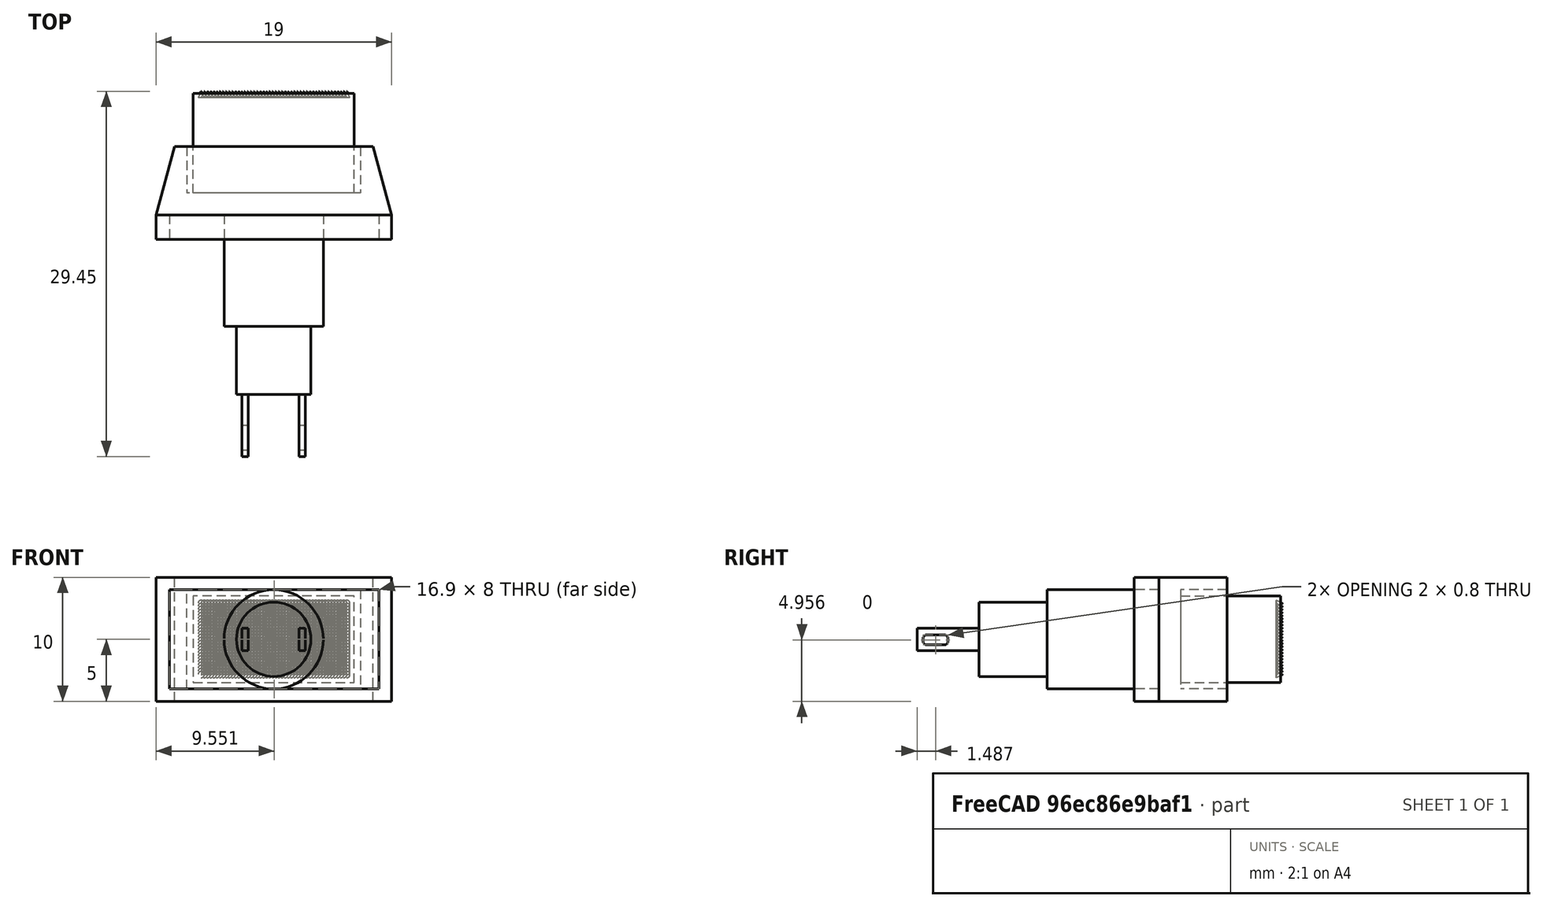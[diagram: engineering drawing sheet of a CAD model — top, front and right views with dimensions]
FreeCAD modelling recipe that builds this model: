
FCSTD DOCUMENT  (FreeCAD 0.18R16110 (Git))
Label: Miyama DS-462 2
License: All rights reserved
LicenseURL: http://en.wikipedia.org/wiki/All_rights_reserved
objects: Sketcher::SketchObject×11, Part::Extrusion×8, Part::Cut×3, Part::Cone×1, Part::FeaturePython×1, Part::Sweep×1
note: 25 computed .brp shape members not serialized (recipe doc carries the construction recipe); baked Part::Feature solids carry a one-line shape summary decoded from their .brp

FEATURE [Sketcher::SketchObject] Sketch
  sketch-geometry (12):
    g0: LineSegment [constr] StartX=-7 StartY=11.8 StartZ=0 EndX=7 EndY=11.8 EndZ=0
    g1: LineSegment [constr] StartX=-9.5 StartY=0 StartZ=0 EndX=9.5 EndY=0 EndZ=0
    g2: LineSegment [constr] StartX=-7 StartY=11.8 StartZ=0 EndX=-7 EndY=7.5 EndZ=0
    g3: LineSegment [constr] StartX=7 StartY=7.5 StartZ=0 EndX=7 EndY=11.8 EndZ=0
    g4: LineSegment [constr] StartX=9.5 StartY=0 StartZ=0 EndX=9.5 EndY=2 EndZ=0
    g5: LineSegment [constr] StartX=9.5 StartY=2 StartZ=0 EndX=7 EndY=7.5 EndZ=0
    g6: LineSegment [constr] StartX=-9.5 StartY=0 StartZ=0 EndX=-9.5 EndY=2 EndZ=0
    g7: LineSegment [constr] StartX=-9.5 StartY=2 StartZ=0 EndX=-7 EndY=7.5 EndZ=0
    g8: LineSegment StartX=-9.5 StartY=2 StartZ=0 EndX=-9.5 EndY=0 EndZ=0
    g9: LineSegment StartX=-9.5 StartY=0 StartZ=0 EndX=9.5 EndY=0 EndZ=0
    g10: LineSegment StartX=9.5 StartY=0 StartZ=0 EndX=9.5 EndY=2 EndZ=0
    g11: LineSegment StartX=9.5 StartY=2 StartZ=0 EndX=-9.5 EndY=2 EndZ=0
  constraints (31):
    c: DistanceX(g0,g0) = 14
    c: DistanceX(g1,g1) = 19
    c: Symmetric(g0,g0,g-2)
    c: Coincident(g2,g0)
    c: Vertical(g2)
    c: Coincident(g3,g0)
    c: Vertical(g3)
    c: DistanceY(g3,g3) = 4.3
    c: Coincident(g4,g1)
    c: Coincident(g5,g4)
    c: Coincident(g7,g6)
    c: Coincident(g7,g2)
    c: Vertical(g6)
    c: Vertical(g4)
    c: DistanceY(g1,g5) = 7.5
    c: Equal(g4,g6)
    c: Coincident(g6,g1)
    c: DistanceY(g4,g4) = 2
    c: PointOnObject(g-1,g1)
    c: Horizontal(g1)
    c: Equal(g7,g5)
    c: Coincident(g3,g5)
    c: Equal(g3,g2)
    c: Coincident(g6,g8)
    c: Coincident(g8,g1)
    c: Coincident(g8,g9)
    c: Coincident(g9,g1)
    c: Coincident(g9,g10)
    c: Coincident(g10,g4)
    c: Coincident(g10,g11)
    c: Coincident(g11,g8)
FEATURE [Sketcher::SketchObject] Sketch001
  sketch-geometry (12):
    g0: LineSegment [constr] StartX=-8 StartY=11.8 StartZ=0 EndX=8 EndY=11.8 EndZ=0
    g1: LineSegment [constr] StartX=-9.5 StartY=0 StartZ=0 EndX=9.5 EndY=0 EndZ=0
    g2: LineSegment [constr] StartX=-8 StartY=11.8 StartZ=0 EndX=-8 EndY=7.5 EndZ=0
    g3: LineSegment [constr] StartX=8 StartY=7.5 StartZ=0 EndX=8 EndY=11.8 EndZ=0
    g4: LineSegment [constr] StartX=9.5 StartY=0 StartZ=0 EndX=9.5 EndY=2 EndZ=0
    g5: LineSegment [constr] StartX=9.5 StartY=2 StartZ=0 EndX=8 EndY=7.5 EndZ=0
    g6: LineSegment [constr] StartX=-9.5 StartY=0 StartZ=0 EndX=-9.5 EndY=2 EndZ=0
    g7: LineSegment [constr] StartX=-9.5 StartY=2 StartZ=0 EndX=-8 EndY=7.5 EndZ=0
    g8: LineSegment StartX=-9.5 StartY=2 StartZ=0 EndX=-8 EndY=7.5 EndZ=0
    g9: LineSegment StartX=-8 StartY=7.5 StartZ=0 EndX=8 EndY=7.5 EndZ=0
    g10: LineSegment StartX=8 StartY=7.5 StartZ=0 EndX=9.5 EndY=2 EndZ=0
    g11: LineSegment StartX=9.5 StartY=2 StartZ=0 EndX=-9.5 EndY=2 EndZ=0
  constraints (31):
    c: DistanceX(g0,g0) = 16
    c: DistanceX(g1,g1) = 19
    c: Symmetric(g0,g0,g-2)
    c: Coincident(g2,g0)
    c: Vertical(g2)
    c: Coincident(g3,g0)
    c: Vertical(g3)
    c: DistanceY(g3,g3) = 4.3
    c: Coincident(g4,g1)
    c: Coincident(g5,g4)
    c: Coincident(g7,g6)
    c: Coincident(g7,g2)
    c: Vertical(g6)
    c: Vertical(g4)
    c: DistanceY(g1,g5) = 7.5
    c: Equal(g4,g6)
    c: Coincident(g6,g1)
    c: DistanceY(g4,g4) = 2
    c: PointOnObject(g-1,g1)
    c: Horizontal(g1)
    c: Equal(g7,g5)
    c: Coincident(g3,g5)
    c: Equal(g3,g2)
    c: Coincident(g6,g8)
    c: Coincident(g8,g2)
    c: Coincident(g8,g9)
    c: Coincident(g9,g10)
    c: Coincident(g10,g4)
    c: Coincident(g10,g11)
    c: Coincident(g11,g8)
    c: Coincident(g9,g3)
FEATURE [Sketcher::SketchObject] Sketch002
  sketch-geometry (12):
    g0: LineSegment [constr] StartX=-7 StartY=11.8 StartZ=0 EndX=7 EndY=11.8 EndZ=0
    g1: LineSegment [constr] StartX=-9.5 StartY=0 StartZ=0 EndX=9.5 EndY=0 EndZ=0
    g2: LineSegment [constr] StartX=-7 StartY=11.8 StartZ=0 EndX=-7 EndY=7.5 EndZ=0
    g3: LineSegment [constr] StartX=7 StartY=7.5 StartZ=0 EndX=7 EndY=11.8 EndZ=0
    g4: LineSegment [constr] StartX=9.5 StartY=0 StartZ=0 EndX=9.5 EndY=2 EndZ=0
    g5: LineSegment [constr] StartX=9.5 StartY=2 StartZ=0 EndX=7 EndY=7.5 EndZ=0
    g6: LineSegment [constr] StartX=-9.5 StartY=0 StartZ=0 EndX=-9.5 EndY=2 EndZ=0
    g7: LineSegment [constr] StartX=-9.5 StartY=2 StartZ=0 EndX=-7 EndY=7.5 EndZ=0
    g8: LineSegment StartX=-7 StartY=11.8 StartZ=0 EndX=-7 EndY=7.5 EndZ=0
    g9: LineSegment StartX=-7 StartY=7.5 StartZ=0 EndX=7 EndY=7.5 EndZ=0
    g10: LineSegment StartX=7 StartY=7.5 StartZ=0 EndX=7 EndY=11.8 EndZ=0
    g11: LineSegment StartX=7 StartY=11.8 StartZ=0 EndX=-7 EndY=11.8 EndZ=0
  constraints (31):
    c: DistanceX(g0,g0) = 14
    c: DistanceX(g1,g1) = 19
    c: Symmetric(g0,g0,g-2)
    c: Coincident(g2,g0)
    c: Vertical(g2)
    c: Coincident(g3,g0)
    c: Vertical(g3)
    c: DistanceY(g3,g3) = 4.3
    c: Coincident(g4,g1)
    c: Coincident(g5,g4)
    c: Coincident(g7,g6)
    c: Coincident(g7,g2)
    c: Vertical(g6)
    c: Vertical(g4)
    c: DistanceY(g1,g5) = 7.5
    c: Equal(g4,g6)
    c: Coincident(g6,g1)
    c: DistanceY(g4,g4) = 2
    c: PointOnObject(g-1,g1)
    c: Horizontal(g1)
    c: Equal(g7,g5)
    c: Coincident(g3,g5)
    c: Equal(g3,g2)
    c: Coincident(g0,g8)
    c: Coincident(g8,g2)
    c: Coincident(g8,g9)
    c: Coincident(g9,g3)
    c: Coincident(g9,g10)
    c: Coincident(g10,g0)
    c: Coincident(g10,g11)
    c: Coincident(g11,g8)
FEATURE [Part::Extrusion] Extrude
  Base = -> Sketch
  Dir = (0,0,1)
  DirMode = 2
  FaceMakerClass = Part::FaceMakerBullseye
  LengthFwd = 10
  LengthRev = 0
  Solid = true
  Symmetric = false
FEATURE [Part::Extrusion] Extrude001
  Base = -> Sketch001
  Dir = (0,0,1)
  DirMode = 2
  FaceMakerClass = Part::FaceMakerBullseye
  LengthFwd = 10
  LengthRev = 0
  Solid = true
  Symmetric = false
FEATURE [Sketcher::SketchObject] Sketch003
  MapMode = 5
  Placement = pos=(0,7.5,0) rot=(0,0.707107,0.707107;3.14159rad)
  Support = -> [Extrude001]
  sketch-geometry (4):
    g0: LineSegment StartX=-7 StartY=9 StartZ=0 EndX=-7 EndY=1 EndZ=0
    g1: LineSegment StartX=-7 StartY=1 StartZ=0 EndX=7 EndY=1 EndZ=0
    g2: LineSegment StartX=7 StartY=1 StartZ=0 EndX=7 EndY=9 EndZ=0
    g3: LineSegment StartX=7 StartY=9 StartZ=0 EndX=-7 EndY=9 EndZ=0
  constraints (8):
    c: Vertical(g0)
    c: Coincident(g0,g1)
    c: Horizontal(g1)
    c: Coincident(g1,g2)
    c: Vertical(g2)
    c: Coincident(g2,g3)
    c: Coincident(g3,g0)
    c: Horizontal(g3)
FEATURE [Part::Extrusion] Extrude002
  Base = -> Sketch003
  Dir = (0,1,-2e-16)
  DirMode = 2
  FaceMakerClass = Part::FaceMakerBullseye
  LengthFwd = -7.5
  LengthRev = 0
  Solid = true
  Symmetric = true
FEATURE [Part::Cut] Cut
  Base = -> Extrude001
  Tool = -> Extrude002
FEATURE [Sketcher::SketchObject] Sketch004
  MapMode = 5
  Placement = pos=(0,3.75,-8e-16) rot=(0,0.707107,0.707107;3.14159rad)
  Support = -> [Cut]
  sketch-geometry (4):
    g0: LineSegment StartX=-6.5 StartY=8.5 StartZ=0 EndX=6.5 EndY=8.5 EndZ=0
    g1: LineSegment StartX=6.5 StartY=8.5 StartZ=0 EndX=6.5 EndY=1.5 EndZ=0
    g2: LineSegment StartX=6.5 StartY=1.5 StartZ=0 EndX=-6.5 EndY=1.5 EndZ=0
    g3: LineSegment StartX=-6.5 StartY=1.5 StartZ=0 EndX=-6.5 EndY=8.5 EndZ=0
  constraints (8):
    c: Coincident(g0,g1)
    c: Coincident(g1,g2)
    c: Coincident(g2,g3)
    c: Coincident(g3,g0)
    c: Horizontal(g0)
    c: Horizontal(g2)
    c: Vertical(g1)
    c: Vertical(g3)
FEATURE [Part::Extrusion] Extrude003
  Base = -> Sketch004
  Dir = (0,1,-2e-16)
  DirMode = 2
  FaceMakerClass = Part::FaceMakerBullseye
  LengthFwd = 8.05
  LengthRev = 0
  Solid = true
  Symmetric = false
FEATURE [Part::Cone] Cone
  Angle = 360
  AttacherType = Attacher::AttachEngine3D
  Height = 0.5
  Placement = pos=(-5.85,11.45,7.9) rot=(1,0,0;4.71239rad)
  Radius1 = 0.25
  Radius2 = 0.01
FEATURE [Part::FeaturePython] Array  # Draft array (typed FeaturePython)
  Angle = 360
  ArrayType = 0
  Axis = (0,0,1)
  Base = -> Cone
  Center = (0,0,0)
  Fuse = false
  IntervalAxis = (0,0,0)
  IntervalX = (0.25,0,0)
  IntervalY = (0,1,0)
  IntervalZ = (0,0,-0.25)
  NumberPolar = 1
  NumberX = 48
  NumberY = 1
  NumberZ = 24
FEATURE [Sketcher::SketchObject] Sketch005
  MapMode = 5
  Placement = pos=(0,0,0) rot=(1,0,0;1.5708rad)
  Support = -> [Extrude]
  sketch-geometry (4):
    g0: LineSegment StartX=-8.39842 StartY=9 StartZ=0 EndX=8.5 EndY=9 EndZ=0
    g1: LineSegment StartX=8.5 StartY=9 StartZ=0 EndX=8.5 EndY=1 EndZ=0
    g2: LineSegment StartX=8.5 StartY=1 StartZ=0 EndX=-8.39842 EndY=1 EndZ=0
    g3: LineSegment StartX=-8.39842 StartY=1 StartZ=0 EndX=-8.39842 EndY=9 EndZ=0
  constraints (8):
    c: Coincident(g0,g1)
    c: Coincident(g1,g2)
    c: Coincident(g2,g3)
    c: Coincident(g3,g0)
    c: Horizontal(g0)
    c: Horizontal(g2)
    c: Vertical(g1)
    c: Vertical(g3)
FEATURE [Part::Extrusion] Extrude004
  Base = -> Sketch005
  Dir = (0,-1,2e-16)
  DirMode = 2
  FaceMakerClass = Part::FaceMakerBullseye
  LengthFwd = 5
  LengthRev = 0
  Solid = true
  Symmetric = true
FEATURE [Part::Cut] Cut001
  Base = -> Extrude
  Tool = -> Extrude004
FEATURE [Sketcher::SketchObject] Sketch006
  MapMode = 5
  Placement = pos=(0,2,0) rot=(1,0,0;1.5708rad)
  Support = -> [Cut]
  sketch-geometry (1):
    g0: Circle CenterX=0 CenterY=5 CenterZ=0 NormalX=0 NormalY=0 NormalZ=1 AngleXU=0 Radius=4
  constraints (2):
    c: PointOnObject(g0,g-2)
    c: Radius(g0) = 4
FEATURE [Sketcher::SketchObject] Sketch007
  ExternalGeometry = -> [Cut]
  sketch-geometry (1):
    g0: LineSegment StartX=0 StartY=2 StartZ=0 EndX=0 EndY=-7 EndZ=0
  constraints (1):
    c: DistanceY(g0,g0) = 9
FEATURE [Part::Sweep] Sweep
  Frenet = false
  Sections = -> [Sketch006]
  Solid = true
  Spine = -> Sketch007
  Transition = 1
FEATURE [Sketcher::SketchObject] Sketch008
  MapMode = 5
  Placement = pos=(0,-7,0) rot=(1,0,0;1.5708rad)
  Support = -> [Sweep]
  sketch-geometry (1):
    g0: Circle CenterX=0 CenterY=5 CenterZ=0 NormalX=0 NormalY=0 NormalZ=1 AngleXU=0 Radius=3
  constraints (1):
    c: PointOnObject(g0,g-2)
FEATURE [Part::Extrusion] Extrude005
  Base = -> Sketch008
  Dir = (0,-1,2e-16)
  DirMode = 2
  FaceMakerClass = Part::FaceMakerBullseye
  LengthFwd = 5.5
  LengthRev = 0
  Solid = true
  Symmetric = false
FEATURE [Sketcher::SketchObject] Sketch009
  MapMode = 5
  Placement = pos=(-1.2e-15,-12.5,2.1e-15) rot=(1,0,0;1.5708rad)
  Support = -> [Extrude005]
  sketch-geometry (10):
    g0: LineSegment StartX=-2.55 StartY=5.89295 StartZ=0 EndX=-2.05 EndY=5.89295 EndZ=0
    g1: LineSegment StartX=-2.05 StartY=5.89295 StartZ=0 EndX=-2.05 EndY=4.09295 EndZ=0
    g2: LineSegment StartX=-2.05 StartY=4.09295 StartZ=0 EndX=-2.55 EndY=4.09295 EndZ=0
    g3: LineSegment StartX=-2.55 StartY=4.09295 StartZ=0 EndX=-2.55 EndY=5.89295 EndZ=0
    g4: LineSegment [constr] StartX=0 StartY=10 StartZ=0 EndX=0 EndY=0 EndZ=0
    g5: LineSegment [constr] StartX=-9.45869 StartY=4.99295 StartZ=0 EndX=9.50951 EndY=4.99295 EndZ=0
    g6: LineSegment StartX=2.55 StartY=5.89295 StartZ=0 EndX=2.55 EndY=4.09295 EndZ=0
    g7: LineSegment StartX=2.05 StartY=5.89295 StartZ=0 EndX=2.55 EndY=5.89295 EndZ=0
    g8: LineSegment StartX=2.05 StartY=4.09295 StartZ=0 EndX=2.05 EndY=5.89295 EndZ=0
    g9: LineSegment StartX=2.55 StartY=4.09295 StartZ=0 EndX=2.05 EndY=4.09295 EndZ=0
  constraints (27):
    c: Coincident(g0,g1)
    c: Coincident(g1,g2)
    c: Coincident(g2,g3)
    c: Coincident(g3,g0)
    c: Horizontal(g0)
    c: Horizontal(g2)
    c: Vertical(g1)
    c: Vertical(g3)
    c: DistanceX(g0,g0) = 0.5
    c: DistanceY(g1,g1) = 1.8
    c: PointOnObject(g4,g-2)
    c: Coincident(g4,g-1)
    c: Horizontal(g5)
    c: DistanceY(g5,g0) = 0.9
    c: DistanceX(g1,g-1) = 2.05
    c: Coincident(g7,g6)
    c: Coincident(g6,g9)
    c: Coincident(g9,g8)
    c: Coincident(g8,g7)
    c: Horizontal(g7)
    c: Horizontal(g9)
    c: Vertical(g6)
    c: Vertical(g8)
    c: DistanceX(g7,g7) = 0.5
    c: DistanceY(g6,g6) = 1.8
    c: DistanceX(g-1,g8) = 2.05
    c: DistanceY(g5,g7) = 0.9
FEATURE [Part::Extrusion] Extrude006
  Base = -> Sketch009
  Dir = (-1e-16,-1,2e-16)
  DirMode = 2
  FaceMakerClass = Part::FaceMakerBullseye
  LengthFwd = 5
  LengthRev = 0
  Solid = true
  Symmetric = false
FEATURE [Sketcher::SketchObject] Sketch010
  MapMode = 5
  Placement = pos=(2.55,-3e-16,0) rot=(0.57735,0.57735,0.57735;2.0944rad)
  Support = -> [Extrude006]
  sketch-geometry (9):
    g0: LineSegment StartX=-16.7272 StartY=5.35582 StartZ=0 EndX=-15.2992 EndY=5.35582 EndZ=0
    g1: LineSegment StartX=-15.0132 StartY=5.06984 StartZ=0 EndX=-15.0132 EndY=4.8418 EndZ=0
    g2: LineSegment StartX=-15.2992 StartY=4.55582 StartZ=0 EndX=-16.7272 EndY=4.55582 EndZ=0
    g3: LineSegment StartX=-17.0132 StartY=4.8418 StartZ=0 EndX=-17.0132 EndY=5.06984 EndZ=0
    g4: LineSegment [constr] StartX=-17.5132 StartY=4 StartZ=0 EndX=-17.5132 EndY=5 EndZ=0
    g5: ArcOfCircle CenterX=-15.2992 CenterY=5.06984 CenterZ=0 NormalX=0 NormalY=0 NormalZ=1 AngleXU=0 Radius=0.285978 StartAngle=1.3e-15 EndAngle=1.5708
    g6: ArcOfCircle CenterX=-16.7272 CenterY=5.06984 CenterZ=0 NormalX=0 NormalY=0 NormalZ=1 AngleXU=0 Radius=0.285978 StartAngle=1.5708 EndAngle=3.14159
    g7: ArcOfCircle CenterX=-15.2992 CenterY=4.8418 CenterZ=0 NormalX=0 NormalY=0 NormalZ=1 AngleXU=0 Radius=0.285978 StartAngle=4.71239 EndAngle=6.28319
    g8: ArcOfCircle CenterX=-16.7272 CenterY=4.8418 CenterZ=0 NormalX=0 NormalY=0 NormalZ=1 AngleXU=0 Radius=0.285978 StartAngle=3.14159 EndAngle=4.71239
  constraints (21):
    c: Horizontal(g0)
    c: Horizontal(g2)
    c: Vertical(g1)
    c: Vertical(g3)
    c: Vertical(g4)
    c: DistanceX(g4) = -17.5132
    c: DistanceY(g4) = 5
    c: Tangent(g1,g5) = 1.5708
    c: Tangent(g0,g5) = 1.5708
    c: Tangent(g0,g6) = 1.5708
    c: Tangent(g3,g6) = 1.5708
    c: Tangent(g1,g7) = 1.5708
    c: Tangent(g2,g7) = 1.5708
    c: Tangent(g2,g8) = 1.5708
    c: Tangent(g3,g8) = 1.5708
    c: DistanceX(g6,g8) = 0
    c: DistanceX(g5,g7) = 0
    c: DistanceX(g4,g3) = 0.5
    c: Equal(g6,g5)
    c: DistanceY(g2,g0) = 0.8
    c: DistanceX(g3,g1) = 2
FEATURE [Part::Extrusion] Extrude007
  Base = -> Sketch010
  Dir = (1,0,0)
  DirMode = 2
  FaceMakerClass = Part::FaceMakerBullseye
  LengthFwd = 20
  LengthRev = 0
  Reversed = true
  Solid = true
  Symmetric = true
FEATURE [Part::Cut] Cut002
  Base = -> Extrude006
  Tool = -> Extrude007
